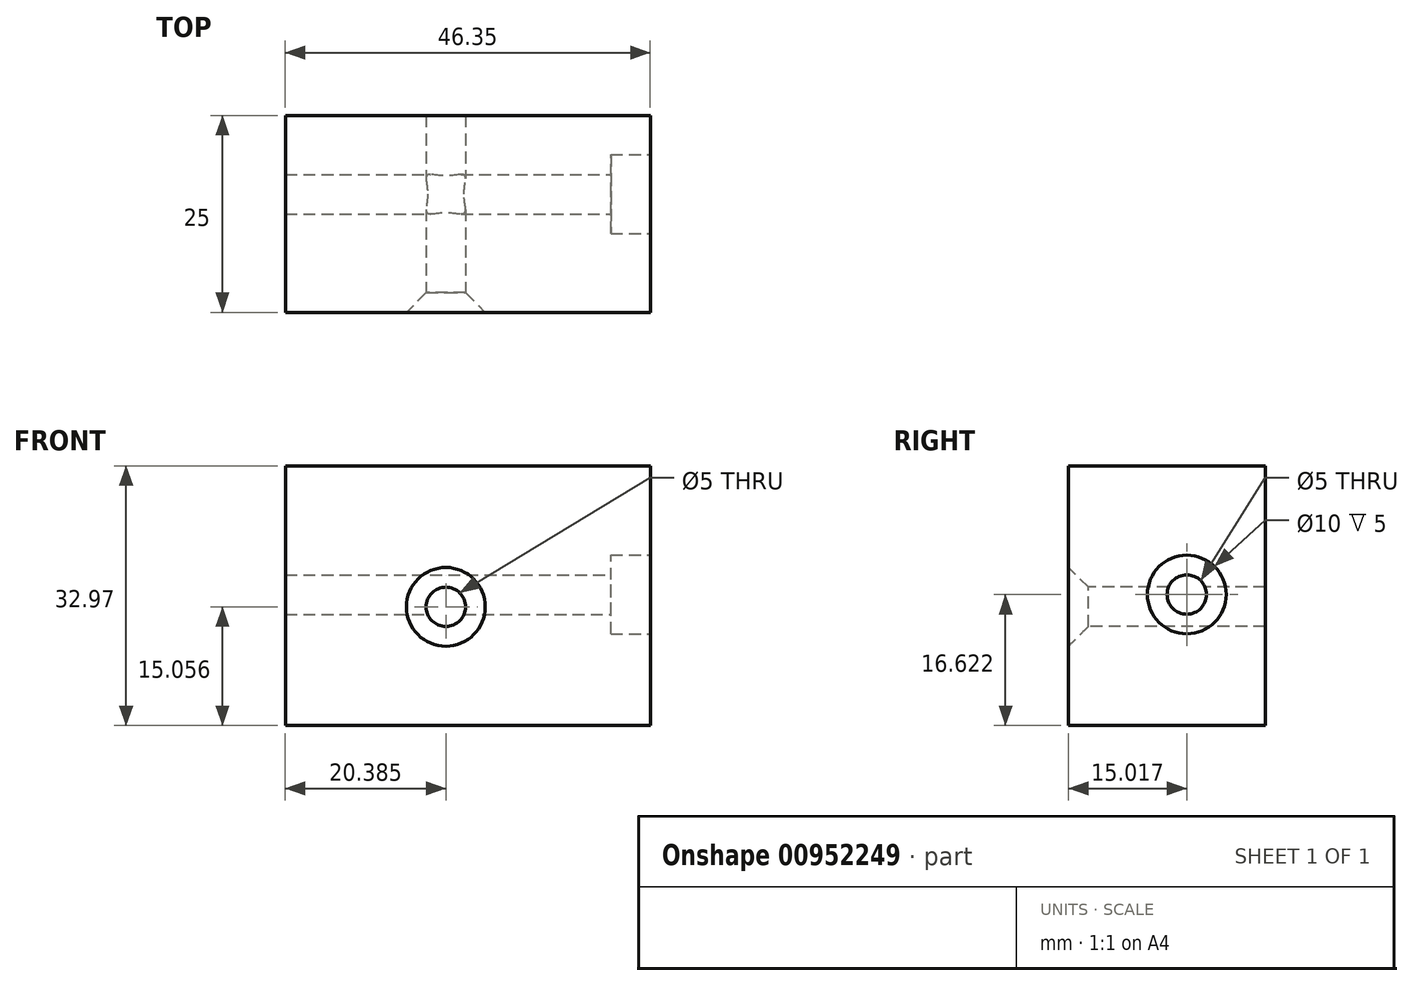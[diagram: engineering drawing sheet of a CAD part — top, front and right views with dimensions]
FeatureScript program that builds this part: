
annotation { "Feature Type Name" : "Feature", "Feature Type Description" : "" }
export const myFeature = defineFeature(function(context is Context, id is Id, definition is map)
    precondition{}
    {
        {
            var Q0;
            Q0=qCreatedBy(makeId("Front.planeOp"),FACE);
            var sketch = newSketch(context, id + "F0", { "sketchPlane" : qUnion([Q0])});
            skLineSegment(sketch, "E0.bottom", {"start": v(24, 32.97) * mm, "end": v(70.34, 32.97) * mm});
            skLineSegment(sketch, "E0.top", {"start": v(24, 0) * mm, "end": v(70.34, 0) * mm});
            skLineSegment(sketch, "E0.left", {"start": v(24, 32.97) * mm, "end": v(24, 0) * mm});
            skLineSegment(sketch, "E0.right", {"start": v(70.34, 32.97) * mm, "end": v(70.34, 0) * mm});
            skSolve(sketch);
        }
        {
            var Q0;
            Q0 = qSketchRegion(id + "F0", true);
            extrude(context, id + "F1", {"entities" : qUnion([Q0]), "depth" : 25 * mm, "offsetDistance" : 25 * mm});
        }
        {
            var Q0;
            Q0=makeQuery(id+"F1.opExtrude","CAP_FACE",FACE,{"disambiguationData":[OSD([sQuery(id+"F0.wireOp",EDGE,"E0.bottom"),sQuery(id+"F0.wireOp",EDGE,"E0.top"),sQuery(id+"F0.wireOp",EDGE,"E0.left"),sQuery(id+"F0.wireOp",EDGE,"E0.right")])],"isStart":false});
            var sketch = newSketch(context, id + "F2", { "sketchPlane" : qUnion([Q0])});
            skPoint(sketch, "E1", {"position": v(44.38, 15.06) * mm});
            skSolve(sketch);
        }
        {
            var Q0;
            Q0=sQuery(id+"F2.wireOp",VERTEX,"E1");
            var Q1;
            Q1=makeQuery(id+"F1.opExtrude","SWEPT_BODY",BODY,{"disambiguationData":[OSD([sQuery(id+"F0.wireOp",EDGE,"E0.bottom"),sQuery(id+"F0.wireOp",EDGE,"E0.top"),sQuery(id+"F0.wireOp",EDGE,"E0.left"),sQuery(id+"F0.wireOp",EDGE,"E0.right")])]});
            hole(context, id + "F3", {"style" : HoleStyle.C_SINK, "endStyle" : HoleEndStyle.THROUGH, "holeDiameter" : 5 * mm, "cSinkDiameter" : 10 * mm, "cSinkAngle" : 90 * degree, "majorDiameter" : 5 * mm, "isTappedThrough" : true, "tappedDepth" : 12 * mm, "tapClearance" : 3, "locations" : qUnion([Q0]), "scope" : qUnion([Q1])});
        }
        {
            var Q0;
            Q0=makeQuery(id+"F1.opExtrude","SWEPT_FACE",FACE,{"disambiguationData":[OSD([sQuery(id+"F0.wireOp",EDGE,"E0.right")])]});
            var sketch = newSketch(context, id + "F4", { "sketchPlane" : qUnion([Q0])});
            skPoint(sketch, "E2", {"position": v(-9.98, 16.62) * mm});
            skSolve(sketch);
        }
        {
            var Q0;
            Q0=sQuery(id+"F4.wireOp",VERTEX,"E2");
            var Q1;
            Q1=makeQuery(id+"F1.opExtrude","SWEPT_BODY",BODY,{"disambiguationData":[OSD([sQuery(id+"F0.wireOp",EDGE,"E0.bottom"),sQuery(id+"F0.wireOp",EDGE,"E0.top"),sQuery(id+"F0.wireOp",EDGE,"E0.left"),sQuery(id+"F0.wireOp",EDGE,"E0.right")])]});
            hole(context, id + "F5", {"style" : HoleStyle.C_BORE, "endStyle" : HoleEndStyle.THROUGH, "holeDiameter" : 5 * mm, "cBoreDiameter" : 10 * mm, "cBoreDepth" : 5 * mm, "majorDiameter" : 5 * mm, "isTappedThrough" : true, "tappedDepth" : 12 * mm, "tapClearance" : 3, "locations" : qUnion([Q0]), "scope" : qUnion([Q1])});
        }
    });
